# Revit family: Mounting Brackets PPR-05515
name_source: partatom
category: Generic Models
revit_build: Autodesk Revit 2017 (Build: 20190508_0315(x64)
units: mm (PartAtom-declared; Revit-internal decimal feet)

## family parameters
Always vertical = No
Can host rebar = No
Cut with Voids When Loaded = No
Part Type = Normal
Room Calculation Point = No
Round Connector Dimension = Use Diameter
Shared = No
Work Plane-Based = Yes

## types (1)
- B83-PPR
    Assembly Code = 63.0
    Bolt_Material = Brass, Soft Yellow, Welded
    Bolt_Visibility = No
    Bracket Article Number = *User Defined
    Bracket_Width = 15 mm  [stored 0.0492126 ft]
    Default Elevation = 1219 mm
    Define - Bracket Article Number = https://www.veko.com
    Description = Mounting Brackets
    Manufacturer = Veko Lightsystems
    Model = B83-PPR
    Mounting_Material = Aluminum 7175 T73 0 Hot Formed
    PNR-11154 = Yes
    Pendulum Start = 98 mm
    Pendulum Visibility = No

note: [stored X ft] marks values corroborated as IEEE doubles in the binary element streams (Revit-internal decimal feet)

## geometry (parser evidence)
native form markers: Extrusion x1, Sweep x2
no freeform markers — native parametric forms only
